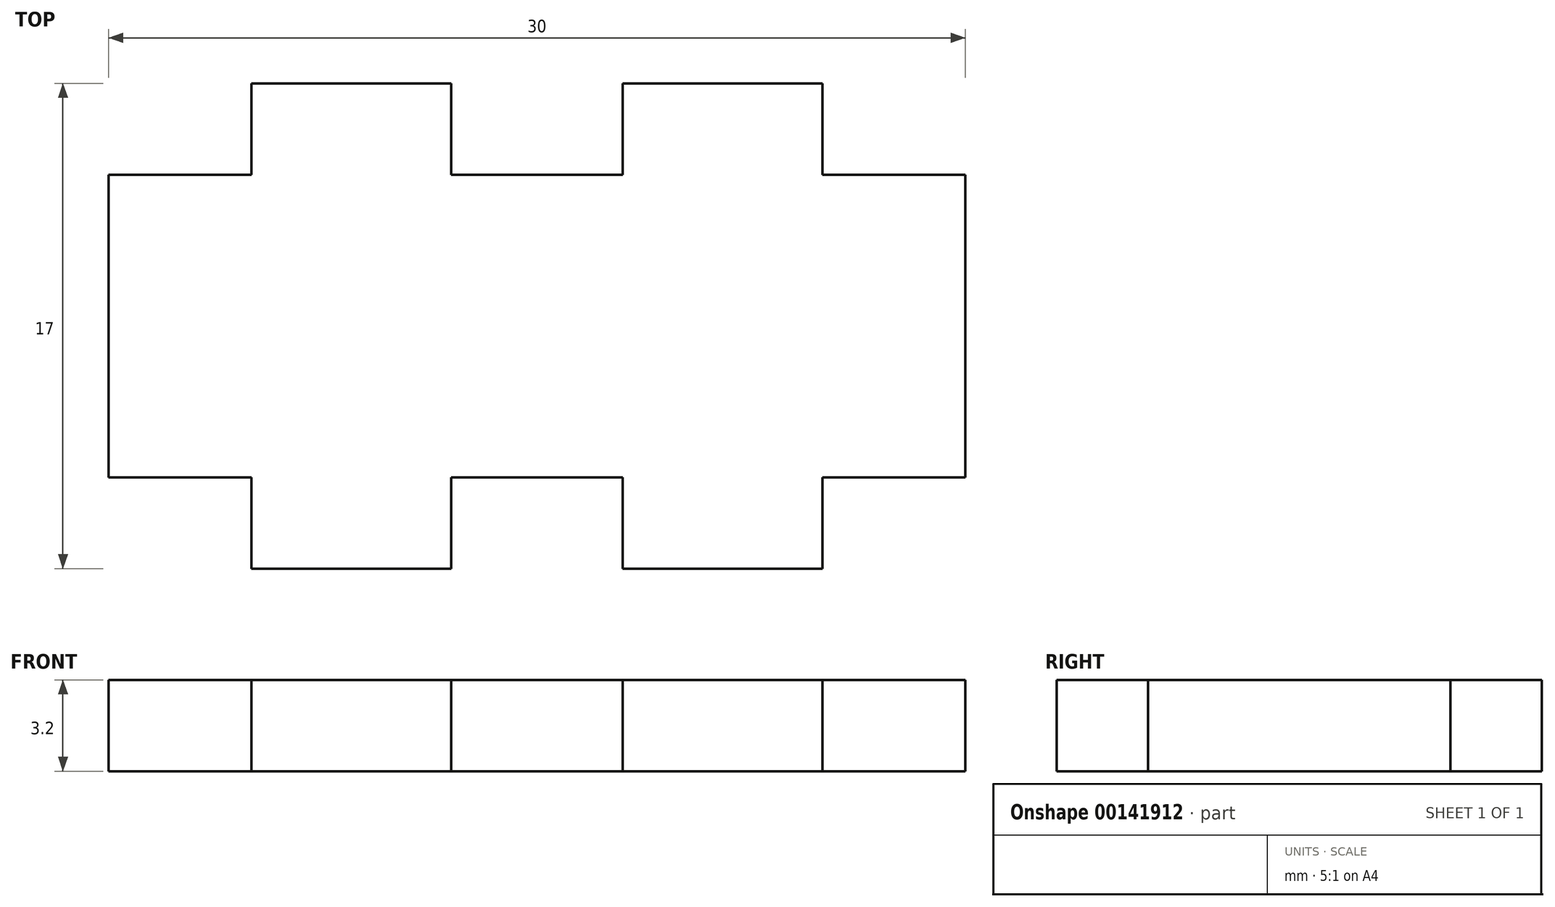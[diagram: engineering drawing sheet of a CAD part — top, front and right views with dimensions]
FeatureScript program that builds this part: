
annotation { "Feature Type Name" : "Feature", "Feature Type Description" : "" }
export const myFeature = defineFeature(function(context is Context, id is Id, definition is map)
    precondition{}
    {
        {
            var Q0;
            Q0=qCreatedBy(makeId("Top.planeOp"),FACE);
            var sketch = newSketch(context, id + "F0", { "sketchPlane" : qUnion([Q0])});
            skLineSegment(sketch, "E0", {"start": v(0, 0) * mm, "end": v(-15, 0) * mm, "construction": true});
            skLineSegment(sketch, "E1", {"start": v(-15, 0) * mm, "end": v(15, 0) * mm, "construction": true});
            skLineSegment(sketch, "E2", {"start": v(-15, 0) * mm, "end": v(-10, 0) * mm, "construction": true});
            skLineSegment(sketch, "E3.bottom", {"start": v(-10, 0) * mm, "end": v(-3, 0) * mm});
            skLineSegment(sketch, "E3.left", {"start": v(-10, 0) * mm, "end": v(-10, -3.2) * mm});
            skLineSegment(sketch, "E3.right", {"start": v(-3, 0) * mm, "end": v(-3, -3.2) * mm});
            skLineSegment(sketch, "E4", {"start": v(-3, 0) * mm, "end": v(3, 0) * mm, "construction": true});
            skLineSegment(sketch, "E5.bottom", {"start": v(3, 0) * mm, "end": v(10, 0) * mm});
            skLineSegment(sketch, "E5.left", {"start": v(3, 0) * mm, "end": v(3, -3.2) * mm});
            skLineSegment(sketch, "E5.right", {"start": v(10, 0) * mm, "end": v(10, -3.2) * mm});
            skLineSegment(sketch, "E6", {"start": v(-10, -3.2) * mm, "end": v(-15, -3.2) * mm, "construction": true});
            skLineSegment(sketch, "E7", {"start": v(-15, -3.2) * mm, "end": v(15, -3.2) * mm, "construction": true});
            skLineSegment(sketch, "E8", {"start": v(-15, -3.2) * mm, "end": v(-10, -3.2) * mm});
            skLineSegment(sketch, "E9", {"start": v(-3, -3.2) * mm, "end": v(3, -3.2) * mm});
            skLineSegment(sketch, "E10", {"start": v(10, -3.2) * mm, "end": v(15, -3.2) * mm});
            skLineSegment(sketch, "E11", {"start": v(-15, 0) * mm, "end": v(-15, -17) * mm, "construction": true});
            skLineSegment(sketch, "E12", {"start": v(-15, -17) * mm, "end": v(-15, -13.8) * mm, "construction": true});
            skLineSegment(sketch, "E13", {"start": v(-15, -13.8) * mm, "end": v(15, -13.8) * mm, "construction": true});
            skLineSegment(sketch, "E14", {"start": v(-15, -3.2) * mm, "end": v(-15, -13.8) * mm});
            skLineSegment(sketch, "E15", {"start": v(-15, -13.8) * mm, "end": v(-10, -13.8) * mm});
            skLineSegment(sketch, "E16", {"start": v(-10, -13.8) * mm, "end": v(-10, -17) * mm});
            skLineSegment(sketch, "E17", {"start": v(-10, -17) * mm, "end": v(-3, -17) * mm});
            skLineSegment(sketch, "E18", {"start": v(-3, -17) * mm, "end": v(-3, -13.8) * mm});
            skLineSegment(sketch, "E19", {"start": v(-3, -13.8) * mm, "end": v(3, -13.8) * mm});
            skLineSegment(sketch, "E20", {"start": v(3, -13.8) * mm, "end": v(3, -17) * mm});
            skLineSegment(sketch, "E21", {"start": v(3, -17) * mm, "end": v(10, -17) * mm});
            skLineSegment(sketch, "E22", {"start": v(10, -17) * mm, "end": v(10, -13.8) * mm});
            skLineSegment(sketch, "E23", {"start": v(10, -13.8) * mm, "end": v(15, -13.8) * mm});
            skLineSegment(sketch, "E24", {"start": v(15, -13.8) * mm, "end": v(15, -3.2) * mm});
            skSolve(sketch);
        }
        {
            var Q0;
            Q0=makeQuery(id+"F0.imprint","IMPRINT",FACE,{"disambiguationData":[TD([[makeQuery(id+"F0.imprint","IMPRINT",EDGE,{"derivedFrom":sQuery(id+"F0.wireOp",EDGE,"E3.bottom")}),-1.0]])]});
            extrude(context, id + "F1", {"entities" : qUnion([Q0]), "endBound" : BoundingType.SYMMETRIC, "depth" : 3.2 * mm});
        }
    });
